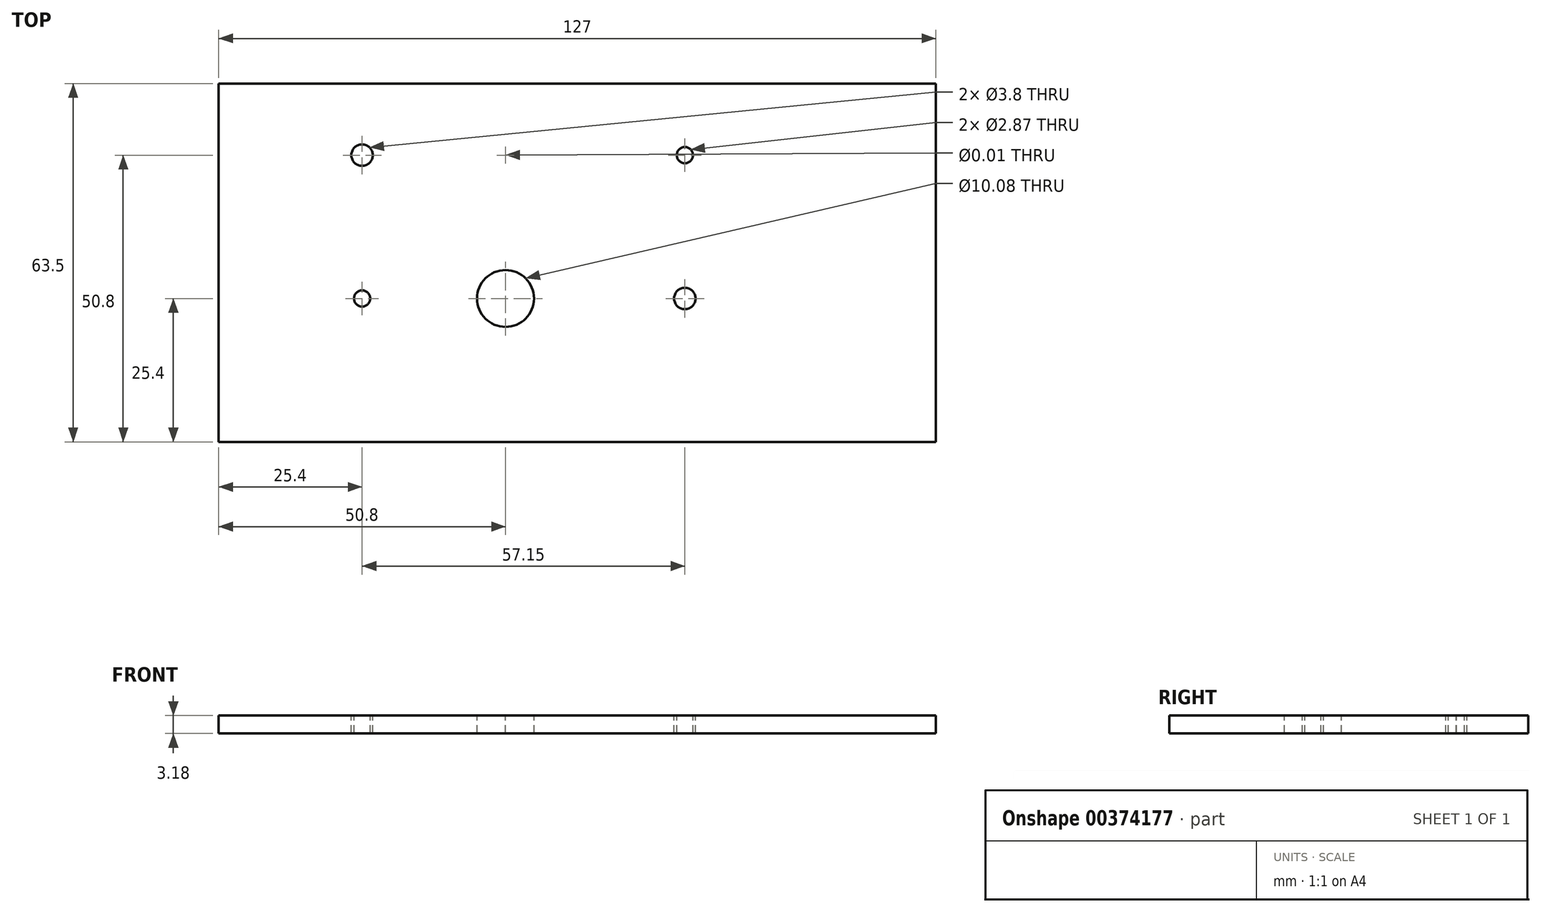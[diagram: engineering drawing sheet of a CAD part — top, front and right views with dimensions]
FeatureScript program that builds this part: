
annotation { "Feature Type Name" : "Feature", "Feature Type Description" : "" }
export const myFeature = defineFeature(function(context is Context, id is Id, definition is map)
    precondition{}
    {
        {
            var Q0;
            Q0=qCreatedBy(makeId("Top.planeOp"),FACE);
            var sketch = newSketch(context, id + "F0", { "sketchPlane" : qUnion([Q0])});
            skLineSegment(sketch, "E0.bottom", {"start": v(0, 0) * mm, "end": v(127, 0) * mm});
            skLineSegment(sketch, "E0.top", {"start": v(0, 63.5) * mm, "end": v(127, 63.5) * mm});
            skLineSegment(sketch, "E0.left", {"start": v(0, 0) * mm, "end": v(0, 63.5) * mm});
            skLineSegment(sketch, "E0.right", {"start": v(127, 0) * mm, "end": v(127, 63.5) * mm});
            skSolve(sketch);
        }
        {
            var Q0;
            Q0 = qSketchRegion(id + "F0", true);
            extrude(context, id + "F1", {"entities" : qUnion([Q0]), "depth" : 3.17 * mm});
        }
        {
            var Q0;
            Q0=makeQuery(id+"F1.opExtrude","CAP_FACE",FACE,{"disambiguationData":[OSD([sQuery(id+"F0.wireOp",EDGE,"E0.bottom"),sQuery(id+"F0.wireOp",EDGE,"E0.top"),sQuery(id+"F0.wireOp",EDGE,"E0.left"),sQuery(id+"F0.wireOp",EDGE,"E0.right")])],"isStart":false});
            var sketch = newSketch(context, id + "F2", { "sketchPlane" : qUnion([Q0])});
            skCircle(sketch, "E1", {"center": v(25.4, 50.8) * mm, "radius": 4.76 * mm});
            skCircle(sketch, "E2", {"center": v(25.4, 25.4) * mm, "radius": 3.18 * mm});
            skCircle(sketch, "E3", {"center": v(50.8, 50.8) * mm, "radius": 6.35 * mm});
            skCircle(sketch, "E4", {"center": v(50.8, 25.4) * mm, "radius": 9.53 * mm});
            skCircle(sketch, "E5", {"center": v(82.55, 50.8) * mm, "radius": 3.18 * mm});
            skCircle(sketch, "E6", {"center": v(82.55, 25.4) * mm, "radius": 4.76 * mm});
            skSolve(sketch);
        }
        {
            var Q0;
            Q0=sQuery(id+"F2.wireOp",VERTEX,"E1.center");
            var Q1;
            Q1=sQuery(id+"F2.wireOp",VERTEX,"E6.center");
            var Q2;
            Q2=makeQuery(id+"F1.opExtrude","SWEPT_BODY",BODY,{"disambiguationData":[OSD([sQuery(id+"F0.wireOp",EDGE,"E0.bottom"),sQuery(id+"F0.wireOp",EDGE,"E0.top"),sQuery(id+"F0.wireOp",EDGE,"E0.left"),sQuery(id+"F0.wireOp",EDGE,"E0.right")])]});
            hole(context, id + "F3", {"style" : HoleStyle.SIMPLE, "endStyle" : HoleEndStyle.THROUGH, "standardTappedOrClearance" : lookupTablePath({ "standard" : "ANSI", "engagement" : "75%", "pitch" : "24 tpi", "size" : "#10", "type" : "Tapped" }), "standardBlindInLast" : lookupTablePath({ "standard" : "ANSI", "engagement" : "75%", "pitch" : "24 tpi", "size" : "#10", "type" : "Tapped" }), "holeDiameter" : 3.8 * mm, "showTappedDepth" : true, "isTappedThrough" : true, "tappedDepth" : 12.7 * mm, "tapClearance" : 3, "locations" : qUnion([Q0, Q1]), "scope" : qUnion([Q2]), "majorDiameter" : 4.83 * mm});
        }
        {
            var Q0;
            Q0=sQuery(id+"F2.wireOp",VERTEX,"E2.center");
            var Q1;
            Q1=sQuery(id+"F2.wireOp",VERTEX,"E5.center");
            var Q2;
            Q2=makeQuery(id+"F1.opExtrude","SWEPT_BODY",BODY,{"disambiguationData":[OSD([sQuery(id+"F0.wireOp",EDGE,"E0.bottom"),sQuery(id+"F0.wireOp",EDGE,"E0.top"),sQuery(id+"F0.wireOp",EDGE,"E0.left"),sQuery(id+"F0.wireOp",EDGE,"E0.right")])]});
            hole(context, id + "F4", {"style" : HoleStyle.SIMPLE, "endStyle" : HoleEndStyle.THROUGH, "standardTappedOrClearance" : lookupTablePath({ "standard" : "ANSI", "engagement" : "75%", "pitch" : "40 tpi", "size" : "#6", "type" : "Tapped" }), "standardBlindInLast" : lookupTablePath({ "standard" : "ANSI", "engagement" : "75%", "pitch" : "40 tpi", "size" : "#6", "type" : "Tapped" }), "holeDiameter" : 2.87 * mm, "showTappedDepth" : true, "isTappedThrough" : true, "tappedDepth" : 12.7 * mm, "tapClearance" : 3, "locations" : qUnion([Q0, Q1]), "scope" : qUnion([Q2]), "majorDiameter" : 3.5 * mm});
        }
        {
            var Q0;
            Q0=sQuery(id+"F2.wireOp",VERTEX,"E3.center");
            var Q1;
            Q1=makeQuery(id+"F1.opExtrude","SWEPT_BODY",BODY,{"disambiguationData":[OSD([sQuery(id+"F0.wireOp",EDGE,"E0.bottom"),sQuery(id+"F0.wireOp",EDGE,"E0.top"),sQuery(id+"F0.wireOp",EDGE,"E0.left"),sQuery(id+"F0.wireOp",EDGE,"E0.right")])]});
            hole(context, id + "F5", {"style" : HoleStyle.SIMPLE, "endStyle" : HoleEndStyle.THROUGH, "standardTappedOrClearance" : lookupTablePath({ "standard" : "ANSI", "size" : "11/32 (0.34)", "type" : "Drilled" }), "standardBlindInLast" : lookupTablePath({ "standard" : "ANSI", "size" : "11/32", "type" : "Drilled" }), "holeDiameter" : 11 / 812.8 * mm, "isTappedThrough" : true, "tappedDepth" : 12.7 * mm, "tapClearance" : 3, "locations" : qUnion([Q0]), "scope" : qUnion([Q1])});
        }
        {
            var Q0;
            Q0=sQuery(id+"F2.wireOp",VERTEX,"E4.center");
            var Q1;
            Q1=makeQuery(id+"F1.opExtrude","SWEPT_BODY",BODY,{"disambiguationData":[OSD([sQuery(id+"F0.wireOp",EDGE,"E0.bottom"),sQuery(id+"F0.wireOp",EDGE,"E0.top"),sQuery(id+"F0.wireOp",EDGE,"E0.left"),sQuery(id+"F0.wireOp",EDGE,"E0.right")])]});
            hole(context, id + "F6", {"style" : HoleStyle.SIMPLE, "endStyle" : HoleEndStyle.THROUGH, "standardTappedOrClearance" : lookupTablePath({ "standard" : "ANSI", "fit" : "Normal (ASME)", "size" : "3/8", "type" : "Clearance" }), "standardBlindInLast" : lookupTablePath({ "fit" : "Free", "standard" : "ANSI", "size" : "3/8", "type" : "Clearance" }), "holeDiameter" : 10.08 * mm, "isTappedThrough" : true, "tappedDepth" : 12.7 * mm, "tapClearance" : 3, "locations" : qUnion([Q0]), "scope" : qUnion([Q1])});
        }
    });
